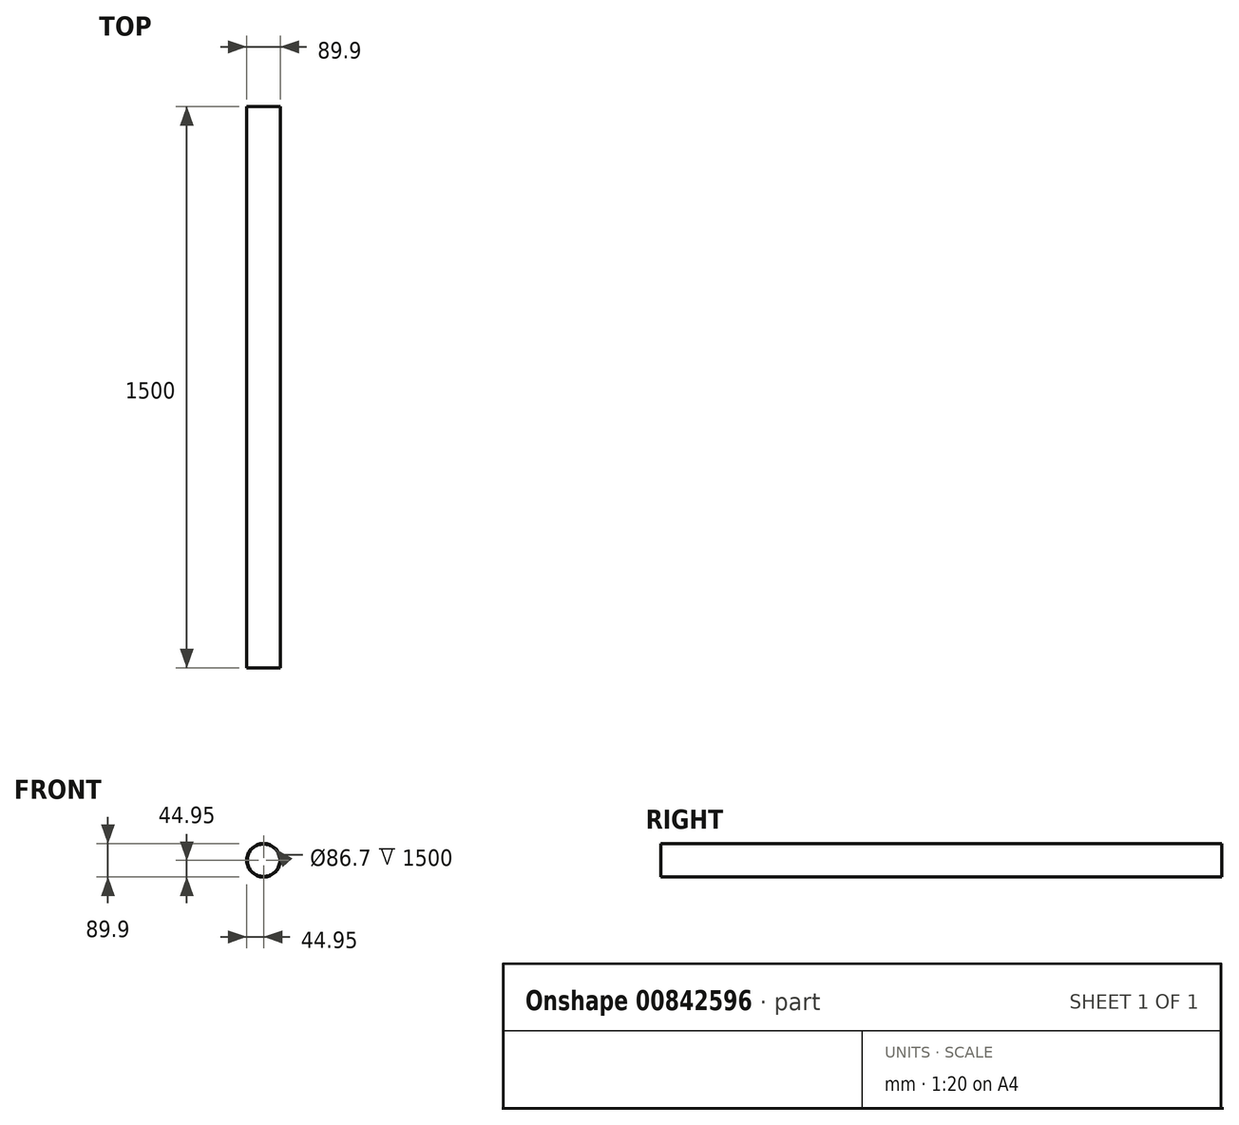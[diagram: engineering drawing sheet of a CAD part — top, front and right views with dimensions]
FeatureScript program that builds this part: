
annotation { "Feature Type Name" : "Feature", "Feature Type Description" : "" }
export const myFeature = defineFeature(function(context is Context, id is Id, definition is map)
    precondition{}
    {
        {
            var Q0;
            Q0=qCreatedBy(makeId("Front.planeOp"),FACE);
            var sketch = newSketch(context, id + "F0", { "sketchPlane" : qUnion([Q0])});
            skCircle(sketch, "E0", {"center": v(0, 0) * mm, "radius": 44.95 * mm});
            skCircle(sketch, "E1", {"center": v(0, 0) * mm, "radius": 43.35 * mm});
            skSolve(sketch);
        }
        {
            var Q0;
            Q0 = qSketchRegion(id + "F0", true);
            extrude(context, id + "F1", {"entities" : qUnion([Q0]), "oppositeDirection" : true, "depth" : 1500 * mm, "offsetDistance" : 25 * mm});
        }
    });
